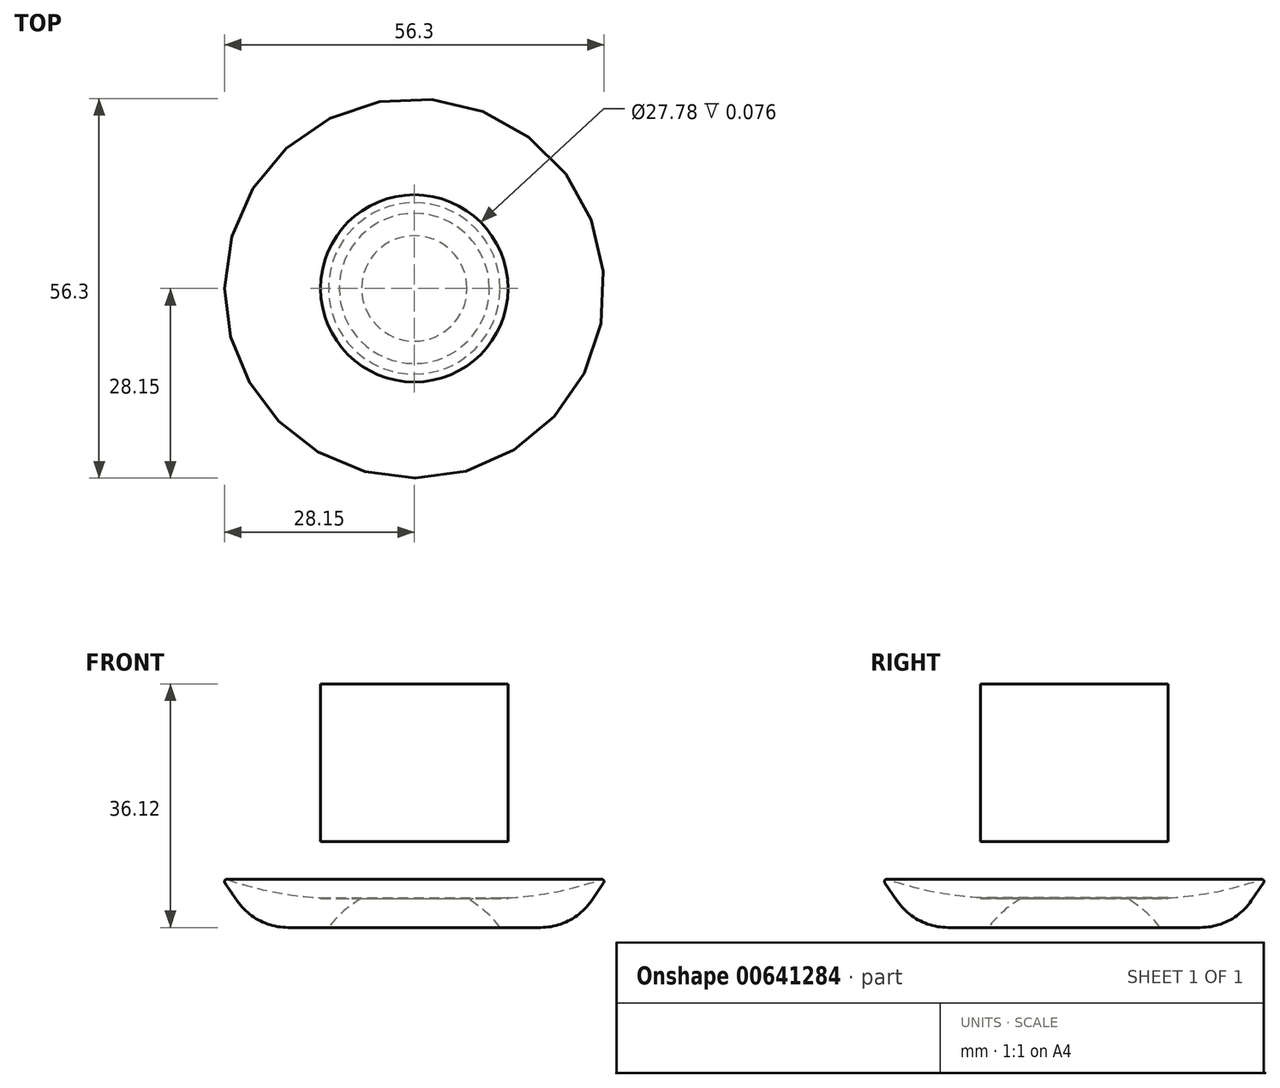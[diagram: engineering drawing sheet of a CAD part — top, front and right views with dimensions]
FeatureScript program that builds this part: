
annotation { "Feature Type Name" : "Feature", "Feature Type Description" : "" }
export const myFeature = defineFeature(function(context is Context, id is Id, definition is map)
    precondition{}
    {
        {
            var Q0;
            Q0=qCreatedBy(makeId("Front.planeOp"),FACE);
            var sketch = newSketch(context, id + "F0", { "sketchPlane" : qUnion([Q0])});
            skArc(sketch, "E0", {"start": v(-15.88, 0) * mm, "mid": v(0, 15.88) * mm, "end": v(15.88, 0) * mm});
            skLineSegment(sketch, "E1", {"start": v(-12.72, 9.5) * mm, "end": v(-18.71, 9.5) * mm});
            skArc(sketch, "E2", {"start": v(-26.26, 13.46) * mm, "mid": v(-22.97, 10.55) * mm, "end": v(-18.71, 9.5) * mm});
            skLineSegment(sketch, "E3", {"start": v(-26.26, 13.46) * mm, "end": v(-28.09, 16.12) * mm});
            skLineSegment(sketch, "E4", {"start": v(0, 15.88) * mm, "end": v(0, 45.62) * mm});
            skPoint(sketch, "E4.endSnap0", {"position": v(0, 15.88) * mm});
            skLineSegment(sketch, "E5", {"start": v(0, 45.62) * mm, "end": v(-13.9, 45.62) * mm});
            skLineSegment(sketch, "E6", {"start": v(-13.9, 45.62) * mm, "end": v(-13.9, 13.82) * mm});
            skLineSegment(sketch, "E7", {"start": v(-13.9, 13.82) * mm, "end": v(-7.82, 13.82) * mm});
            skLineSegment(sketch, "E8", {"start": v(-11.13, 13.82) * mm, "end": v(-13.9, 13.82) * mm});
            skArc(sketch, "E9", {"start": v(-27.7, 16.63) * mm, "mid": v(-19.53, 14.52) * mm, "end": v(-11.13, 13.82) * mm});
            skPoint(sketch, "E10.visualSharp", {"position": v(-28.69, 16.98) * mm});
            skArc(sketch, "E10.filletArc", {"start": v(-27.7, 16.63) * mm, "mid": v(-28.08, 16.51) * mm, "end": v(-28.09, 16.12) * mm});
            skLineSegment(sketch, "E11", {"start": v(-13.9, 22.23) * mm, "end": v(0, 22.23) * mm});
            skSolve(sketch);
        }
        {
            var Q0;
            {var subQ0=sQuery(id+"F0.wireOp",EDGE,"E1");Q0=makeQuery(id+"F0.imprint","IMPRINT",FACE,{"disambiguationData":[TD([[makeQuery(id+"F0.imprint","IMPRINT",EDGE,{"derivedFrom":subQ0}),-1.0]])]});}
            var Q1;
            {var subQ0=sQuery(id+"F0.wireOp",EDGE,"E5");Q1=makeQuery(id+"F0.imprint","IMPRINT",FACE,{"disambiguationData":[TD([[makeQuery(id+"F0.imprint","IMPRINT",EDGE,{"derivedFrom":subQ0}),1.0]])]});}
            var Q2;
            Q2=sQuery(id+"F0.wireOp",EDGE,"E4");
            revolve(context, id + "F1", {"entities" : qUnion([Q0, Q1]), "axis" : qUnion([Q2]), "revolveType" : RevolveType.FULL});
        }
        {
            var Q0;
            Q0=qCreatedBy(makeId("Front.planeOp"),FACE);
            var sketch = newSketch(context, id + "F2", { "sketchPlane" : qUnion([Q0])});
            skArc(sketch, "E12", {"start": v(-31.75, 0) * mm, "mid": v(0, 31.75) * mm, "end": v(31.75, 0) * mm});
            skLineSegment(sketch, "E13", {"start": v(0, 31.75) * mm, "end": v(0, 41.01) * mm});
            skLineSegment(sketch, "E14", {"start": v(0, 41.01) * mm, "end": v(-24.6, 41.01) * mm});
            skLineSegment(sketch, "E15", {"start": v(-24.6, 41.01) * mm, "end": v(-24.6, 24.32) * mm});
            skLineSegment(sketch, "E16", {"start": v(-24.6, 24.32) * mm, "end": v(-20.41, 24.32) * mm});
            skSolve(sketch);
        }
        {
            var Q0;
            {var subQ0=sQuery(id+"F0.wireOp",EDGE,"E7");Q0=makeQuery(id+"F0.imprint","IMPRINT",FACE,{"disambiguationData":[TD([[makeQuery(id+"F0.imprint","IMPRINT",EDGE,{"derivedFrom":subQ0}),1.0]])]});}
            var Q1;
            Q1=sQuery(id+"F2.wireOp",EDGE,"E13");
            revolve(context, id + "F3", {"entities" : qUnion([Q0]), "axis" : qUnion([Q1]), "revolveType" : RevolveType.FULL});
        }
    });
